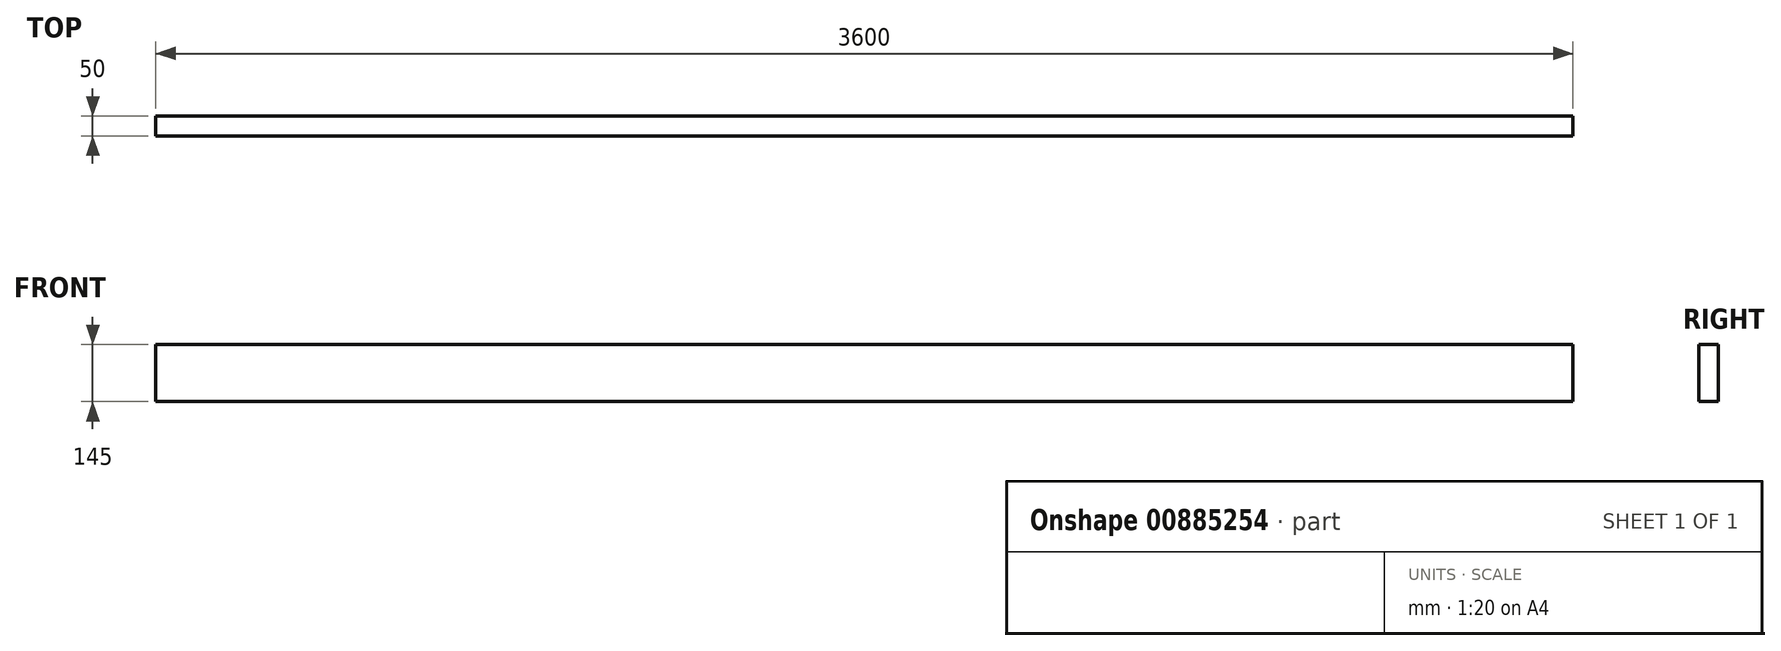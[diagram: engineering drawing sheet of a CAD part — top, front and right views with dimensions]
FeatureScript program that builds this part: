
annotation { "Feature Type Name" : "Feature", "Feature Type Description" : "" }
export const myFeature = defineFeature(function(context is Context, id is Id, definition is map)
    precondition{}
    {
        {
            var Q0;
            Q0=qCreatedBy(makeId("Right.planeOp"),FACE);
            var sketch = newSketch(context, id + "F0", { "sketchPlane" : qUnion([Q0])});
            skLineSegment(sketch, "E0.bottom", {"start": v(19.83, 104.45) * mm, "end": v(-30.17, 104.45) * mm});
            skLineSegment(sketch, "E0.top", {"start": v(19.83, -40.55) * mm, "end": v(-30.17, -40.55) * mm});
            skLineSegment(sketch, "E0.left", {"start": v(19.83, 104.45) * mm, "end": v(19.83, -40.55) * mm});
            skLineSegment(sketch, "E0.right", {"start": v(-30.17, 104.45) * mm, "end": v(-30.17, -40.55) * mm});
            skSolve(sketch);
        }
        {
            var Q0;
            Q0=makeQuery(id+"F0.imprint","IMPRINT",FACE,{"disambiguationData":[TD([[makeQuery(id+"F0.imprint","IMPRINT",EDGE,{"derivedFrom":sQuery(id+"F0.wireOp",EDGE,"E0.bottom")}),1.0]])]});
            extrude(context, id + "F1", {"entities" : qUnion([Q0]), "depth" : 3600 * mm, "offsetDistance" : 25 * mm});
        }
    });
